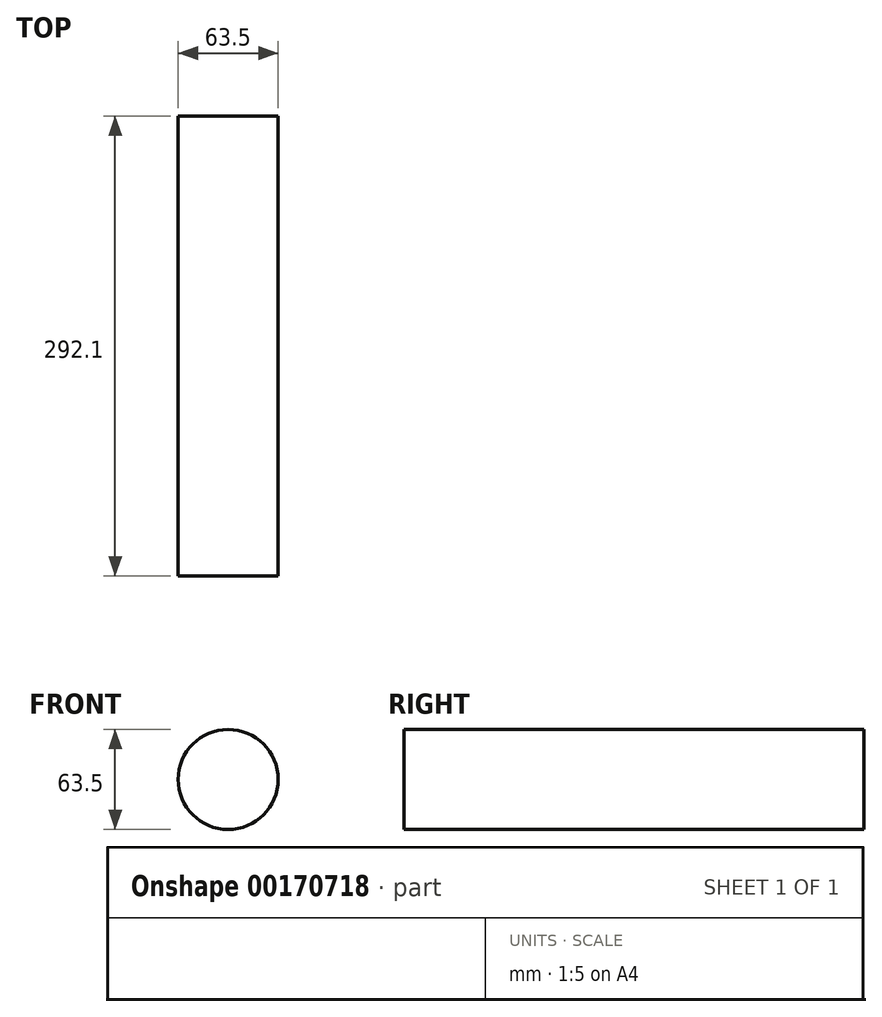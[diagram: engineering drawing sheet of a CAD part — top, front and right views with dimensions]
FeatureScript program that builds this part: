
annotation { "Feature Type Name" : "Feature", "Feature Type Description" : "" }
export const myFeature = defineFeature(function(context is Context, id is Id, definition is map)
    precondition{}
    {
        {
            var Q0;
            Q0=qCreatedBy(makeId("Front.planeOp"),FACE);
            var sketch = newSketch(context, id + "F0", { "sketchPlane" : qUnion([Q0])});
            skCircle(sketch, "E0", {"center": v(0, 0) * mm, "radius": 31.75 * mm});
            skSolve(sketch);
        }
        {
            var Q0;
            Q0=makeQuery(id+"F0.imprint","IMPRINT",FACE,{"disambiguationData":[TD([[makeQuery(id+"F0.imprint","IMPRINT",EDGE,{"derivedFrom":sQuery(id+"F0.wireOp",EDGE,"E0")}),1.0]])]});
            extrude(context, id + "F1", {"entities" : qUnion([Q0]), "depth" : 292.1 * mm});
        }
    });
